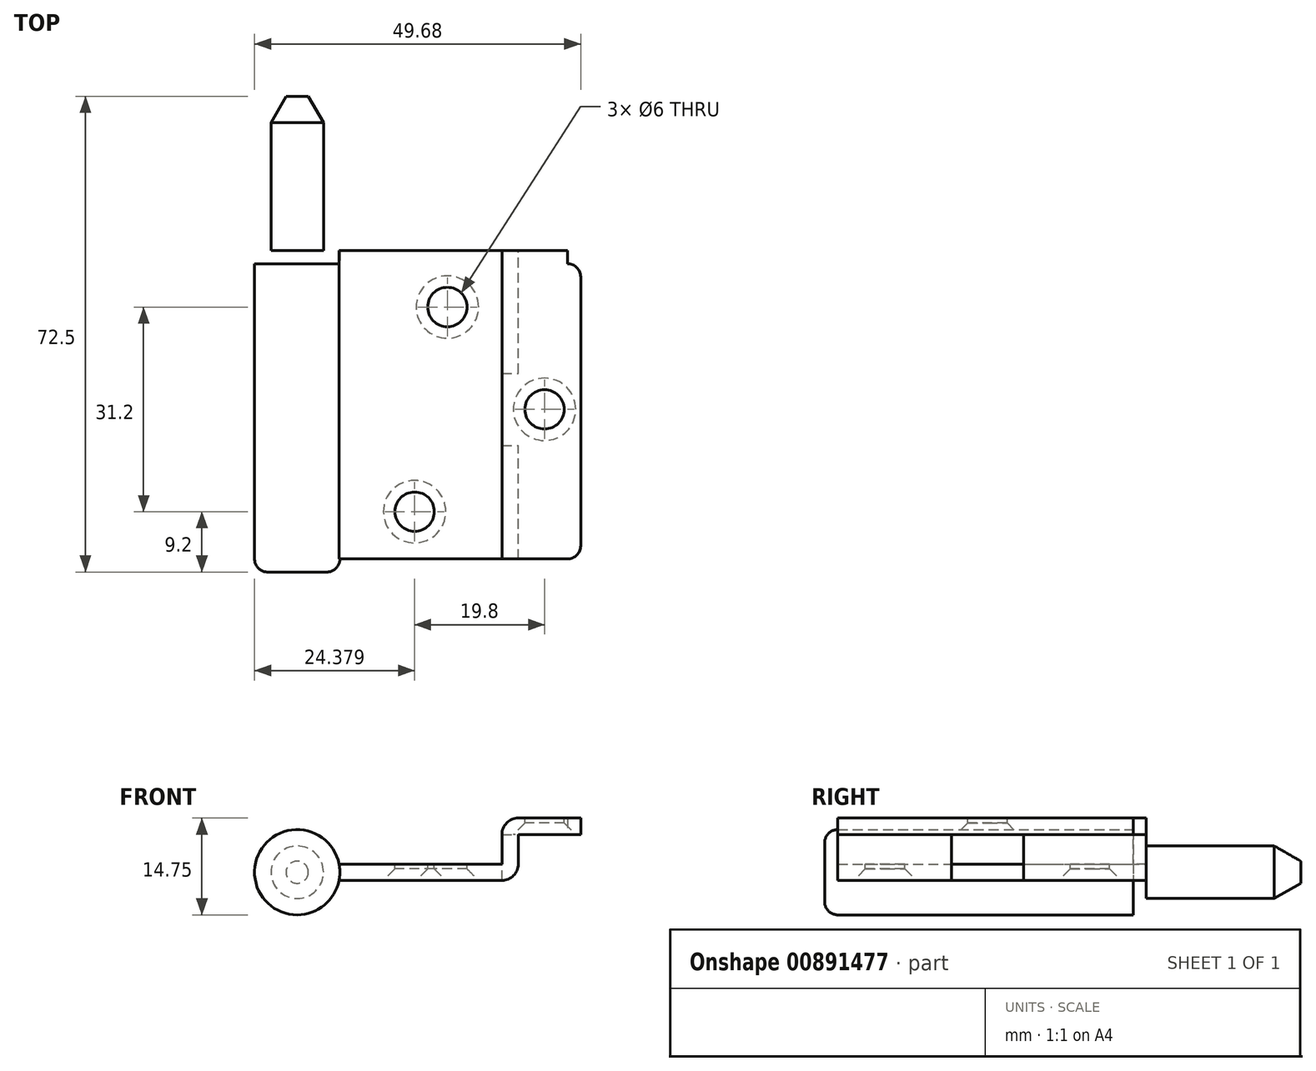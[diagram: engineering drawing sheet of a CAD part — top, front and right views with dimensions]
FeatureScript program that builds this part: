
annotation { "Feature Type Name" : "Feature", "Feature Type Description" : "" }
export const myFeature = defineFeature(function(context is Context, id is Id, definition is map)
    precondition{}
    {
        {
            var Q0;
            Q0=qCreatedBy(makeId("Front.planeOp"),FACE);
            var sketch = newSketch(context, id + "F0", { "sketchPlane" : qUnion([Q0])});
            skArc(sketch, "E0", {"start": v(6.38, 1.25) * mm, "mid": v(-6.5, 0) * mm, "end": v(6.38, -1.25) * mm});
            skLineSegment(sketch, "E1", {"start": v(6.38, 1.25) * mm, "end": v(31.18, 1.25) * mm});
            skLineSegment(sketch, "E2", {"start": v(31.18, 8.25) * mm, "end": v(43.18, 8.25) * mm});
            skLineSegment(sketch, "E3", {"start": v(43.18, 8.25) * mm, "end": v(43.18, 5.75) * mm});
            skLineSegment(sketch, "E4", {"start": v(43.18, 5.75) * mm, "end": v(33.68, 5.75) * mm});
            skLineSegment(sketch, "E5", {"start": v(33.68, -1.25) * mm, "end": v(6.38, -1.25) * mm});
            skLineSegment(sketch, "E6", {"start": v(33.68, 5.75) * mm, "end": v(33.68, -1.25) * mm});
            skLineSegment(sketch, "E7", {"start": v(31.18, 8.25) * mm, "end": v(31.18, 1.25) * mm});
            skSolve(sketch);
        }
        {
            var Q0;
            Q0=makeQuery(id+"F0.imprint","IMPRINT",FACE,{"disambiguationData":[TD([[makeQuery(id+"F0.imprint","IMPRINT",EDGE,{"derivedFrom":sQuery(id+"F0.wireOp",EDGE,"E0")}),1.0]])]});
            extrude(context, id + "F1", {"entities" : qUnion([Q0]), "depth" : 45 * mm, "offsetDistance" : 25 * mm});
        }
        {
            var Q0;
            Q0=makeQuery(id+"F1.opExtrude","CAP_EDGE",EDGE,{"disambiguationData":[OSD([sQuery(id+"F0.wireOp",EDGE,"E3")])],"isStart":false});
            var Q1;
            Q1=makeQuery(id+"F1.opExtrude","CAP_EDGE",EDGE,{"disambiguationData":[OSD([sQuery(id+"F0.wireOp",EDGE,"E3")])],"isStart":true});
            fillet(context, id + "F2", {"entities" : qUnion([Q0, Q1]), "radius" : 2 * mm, "tangentPropagation" : true, "allowEdgeOverflow" : false});
        }
        {
            var Q0;
            Q0=makeQuery(id+"F1.opExtrude","SWEPT_EDGE",EDGE,{"disambiguationData":[OSD([sQuery(id+"F0.wireOp",EDGE,"E5"),sQuery(id+"F0.wireOp",EDGE,"E6")])]});
            var Q1;
            Q1=makeQuery(id+"F1.opExtrude","SWEPT_EDGE",EDGE,{"disambiguationData":[OSD([sQuery(id+"F0.wireOp",EDGE,"E2"),sQuery(id+"F0.wireOp",EDGE,"E7")])]});
            fillet(context, id + "F3", {"entities" : qUnion([Q0, Q1]), "radius" : 2.5 * mm, "tangentPropagation" : true, "allowEdgeOverflow" : false});
        }
        {
            var Q0;
            Q0=makeQuery(id+"F1.opExtrude","CAP_FACE",FACE,{"disambiguationData":[OSD([sQuery(id+"F0.wireOp",EDGE,"E0"),sQuery(id+"F0.wireOp",EDGE,"E1"),sQuery(id+"F0.wireOp",EDGE,"WSlHtf5i-U6j4-Ynl4-FoHb-XjoWY4hGSOt6"),sQuery(id+"F0.wireOp",EDGE,"E2"),sQuery(id+"F0.wireOp",EDGE,"E3"),sQuery(id+"F0.wireOp",EDGE,"E4"),sQuery(id+"F0.wireOp",EDGE,"E5"),sQuery(id+"F0.wireOp",EDGE,"dJLKLTg6-jbDR-ftkV-erEf-zidkdKnkohMK"),sQuery(id+"F0.wireOp",EDGE,"M6QVCp6i-pHj4-OTcd-NfKp-MZP8uRFXvbLj"),sQuery(id+"F0.wireOp",EDGE,"RtBS60rh-hvOl-1zH0-KM05-FjQfmGGDyUj7")])],"isStart":true});
            var sketch = newSketch(context, id + "F4", { "sketchPlane" : qUnion([Q0])});
            skCircle(sketch, "E8", {"center": v(0, 0) * mm, "radius": 6.5 * mm});
            skSolve(sketch);
        }
        {
            var Q0;
            {var subQ0=sQuery(id+"F4.wireOp",EDGE,"E8");Q0=makeQuery(id+"F4.imprint","IMPRINT",FACE,{"disambiguationData":[TD([[makeQuery(id+"F4.imprint","IMPRINT",EDGE,{"disambiguationData":[OD(0.0)],"derivedFrom":subQ0}),-1.0]])]});}
            extrude(context, id + "F5", {"entities" : qUnion([Q0]), "operationType" : NewBodyOperationType.ADD, "depth" : 2 * mm, "offsetDistance" : 25 * mm});
        }
        {
            var Q0;
            Q0=makeQuery(id+"F5.opExtrude","CAP_FACE",FACE,{"disambiguationData":[OSD([sQuery(id+"F4.wireOp",EDGE,"E8")])],"isStart":false});
            var sketch = newSketch(context, id + "F6", { "sketchPlane" : qUnion([Q0])});
            skCircle(sketch, "E9", {"center": v(0, 0) * mm, "radius": 4 * mm});
            skSolve(sketch);
        }
        {
            var Q0;
            Q0=makeQuery(id+"F6.imprint","IMPRINT",FACE,{"disambiguationData":[TD([[makeQuery(id+"F6.imprint","IMPRINT",EDGE,{"derivedFrom":sQuery(id+"F6.wireOp",EDGE,"E9")}),1.0]])]});
            extrude(context, id + "F7", {"entities" : qUnion([Q0]), "operationType" : NewBodyOperationType.ADD, "depth" : 23.5 * mm, "offsetDistance" : 25 * mm});
        }
        {
            var Q0;
            Q0=makeQuery(id+"F7.opExtrude","CAP_EDGE",EDGE,{"disambiguationData":[OSD([sQuery(id+"F6.wireOp",EDGE,"E9")])],"isStart":false});
            chamfer(context, id + "F8", {"entities" : qUnion([Q0]), "chamferType" : ChamferType.TWO_OFFSETS, "width1" : 4 * mm, "oppositeDirection" : true, "width2" : 2.31 * mm, "tangentPropagation" : true});
        }
        {
            var Q0;
            Q0=makeQuery(id+"F1.opExtrude","SWEPT_FACE",FACE,{"disambiguationData":[OSD([sQuery(id+"F0.wireOp",EDGE,"E5")])]});
            var sketch = newSketch(context, id + "F9", { "sketchPlane" : qUnion([Q0])});
            skPoint(sketch, "E10", {"position": v(22.88, 6.6) * mm});
            skPoint(sketch, "E11", {"position": v(17.88, 37.8) * mm});
            skSolve(sketch);
        }
        {
            var Q0;
            Q0=sQuery(id+"F9.wireOp",VERTEX,"E10");
            var Q1;
            Q1=sQuery(id+"F9.wireOp",VERTEX,"E11");
            var Q2;
            Q2=sQuery(id+"F1gnd5VNBVrkXNz_1.wireOp",VERTEX,"af38a646-69fc-4794-a32b-26258d2a7c5d");
            var Q3;
            Q3=makeQuery(id+"F1.opExtrude","SWEPT_BODY",BODY,{"disambiguationData":[OSD([sQuery(id+"F0.wireOp",EDGE,"E0"),sQuery(id+"F0.wireOp",EDGE,"E1"),sQuery(id+"F0.wireOp",EDGE,"WSlHtf5i-U6j4-Ynl4-FoHb-XjoWY4hGSOt6"),sQuery(id+"F0.wireOp",EDGE,"E2"),sQuery(id+"F0.wireOp",EDGE,"E3"),sQuery(id+"F0.wireOp",EDGE,"E4"),sQuery(id+"F0.wireOp",EDGE,"E5"),sQuery(id+"F0.wireOp",EDGE,"dJLKLTg6-jbDR-ftkV-erEf-zidkdKnkohMK"),sQuery(id+"F0.wireOp",EDGE,"M6QVCp6i-pHj4-OTcd-NfKp-MZP8uRFXvbLj"),sQuery(id+"F0.wireOp",EDGE,"RtBS60rh-hvOl-1zH0-KM05-FjQfmGGDyUj7")])]});
            hole(context, id + "F10", {"style" : HoleStyle.C_SINK, "endStyle" : HoleEndStyle.THROUGH, "standardTappedOrClearance" : lookupTablePath({ "standard" : "ISO", "size" : "6", "type" : "Drilled" }), "standardBlindInLast" : lookupTablePath({ "standard" : "ISO", "size" : "6", "type" : "Drilled" }), "holeDiameter" : 6 * mm, "cSinkDiameter" : 9.5 * mm, "cSinkAngle" : 90 * degree, "majorDiameter" : 5 * mm, "isTappedThrough" : true, "tappedDepth" : 12 * mm, "tapClearance" : 3, "startFromSketch" : true, "locations" : qUnion([Q0, Q1, Q2]), "scope" : qUnion([Q3])});
        }
        {
            var Q0;
            Q0=makeQuery(id+"F1.opExtrude","CAP_FACE",FACE,{"disambiguationData":[OSD([sQuery(id+"F0.wireOp",EDGE,"E0"),sQuery(id+"F0.wireOp",EDGE,"E1"),sQuery(id+"F0.wireOp",EDGE,"WSlHtf5i-U6j4-Ynl4-FoHb-XjoWY4hGSOt6"),sQuery(id+"F0.wireOp",EDGE,"E2"),sQuery(id+"F0.wireOp",EDGE,"E3"),sQuery(id+"F0.wireOp",EDGE,"E4"),sQuery(id+"F0.wireOp",EDGE,"E5"),sQuery(id+"F0.wireOp",EDGE,"dJLKLTg6-jbDR-ftkV-erEf-zidkdKnkohMK"),sQuery(id+"F0.wireOp",EDGE,"M6QVCp6i-pHj4-OTcd-NfKp-MZP8uRFXvbLj"),sQuery(id+"F0.wireOp",EDGE,"RtBS60rh-hvOl-1zH0-KM05-FjQfmGGDyUj7")])],"isStart":false});
            var sketch = newSketch(context, id + "F11", { "sketchPlane" : qUnion([Q0])});
            skCircle(sketch, "E12", {"center": v(0, 0) * mm, "radius": 6.5 * mm});
            skSolve(sketch);
        }
        {
            var Q0;
            Q0 = qSketchRegion(id + "F11", true);
            extrude(context, id + "F12", {"entities" : qUnion([Q0]), "operationType" : NewBodyOperationType.ADD, "depth" : 2 * mm, "offsetDistance" : 25 * mm});
        }
        {
            var Q0;
            Q0=makeQuery(id+"F12.opExtrude","CAP_EDGE",EDGE,{"disambiguationData":[OSD([sQuery(id+"F11.wireOp",EDGE,"E12")])],"isStart":false});
            fillet(context, id + "F13", {"entities" : qUnion([Q0]), "radius" : 2 * mm, "tangentPropagation" : true, "allowEdgeOverflow" : false});
        }
        {
            var Q0;
            Q0=makeQuery(id+"F1.opExtrude","SWEPT_FACE",FACE,{"disambiguationData":[OSD([sQuery(id+"F0.wireOp",EDGE,"E4")])]});
            var sketch = newSketch(context, id + "F14", { "sketchPlane" : qUnion([Q0])});
            skPoint(sketch, "E13", {"position": v(37.68, 22.2) * mm});
            skLineSegment(sketch, "E14.bottom", {"start": v(31.18, 27.7) * mm, "end": v(36.18, 27.7) * mm});
            skLineSegment(sketch, "E14.top", {"start": v(31.18, 16.7) * mm, "end": v(36.18, 16.7) * mm});
            skLineSegment(sketch, "E14.left", {"start": v(31.18, 27.7) * mm, "end": v(31.18, 16.7) * mm});
            skLineSegment(sketch, "E14.right", {"start": v(36.18, 27.7) * mm, "end": v(36.18, 16.7) * mm});
            skPoint(sketch, "E14.middle", {"position": v(33.68, 22.2) * mm});
            skPoint(sketch, "E14.middle.positionSnap0", {"position": v(33.68, 22.5) * mm});
            skPoint(sketch, "E14.centerSnap0", {"position": v(33.68, 22.5) * mm});
            skSolve(sketch);
        }
        {
            var Q0;
            Q0 = qSketchRegion(id + "F14", true);
            extrude(context, id + "F15", {"entities" : qUnion([Q0]), "operationType" : NewBodyOperationType.REMOVE, "depth" : 25 * mm, "offsetDistance" : 25 * mm});
        }
        {
            var Q0;
            Q0=sQuery(id+"F14.wireOp",VERTEX,"E13");
            var Q1;
            Q1=makeQuery(id+"F1.opExtrude","SWEPT_BODY",BODY,{"disambiguationData":[OSD([sQuery(id+"F0.wireOp",EDGE,"E0"),sQuery(id+"F0.wireOp",EDGE,"E1"),sQuery(id+"F0.wireOp",EDGE,"E2"),sQuery(id+"F0.wireOp",EDGE,"E3"),sQuery(id+"F0.wireOp",EDGE,"E4"),sQuery(id+"F0.wireOp",EDGE,"E5"),sQuery(id+"F0.wireOp",EDGE,"E6"),sQuery(id+"F0.wireOp",EDGE,"E7")])]});
            hole(context, id + "F16", {"style" : HoleStyle.C_SINK, "endStyle" : HoleEndStyle.THROUGH, "standardTappedOrClearance" : lookupTablePath({ "standard" : "ISO", "size" : "6", "type" : "Drilled" }), "standardBlindInLast" : lookupTablePath({ "standard" : "ISO", "size" : "6", "type" : "Drilled" }), "holeDiameter" : 6 * mm, "cSinkDiameter" : 9.5 * mm, "cSinkAngle" : 90 * degree, "majorDiameter" : 5 * mm, "isTappedThrough" : true, "tappedDepth" : 12 * mm, "tapClearance" : 3, "startFromSketch" : true, "locations" : qUnion([Q0]), "scope" : qUnion([Q1])});
        }
    });
